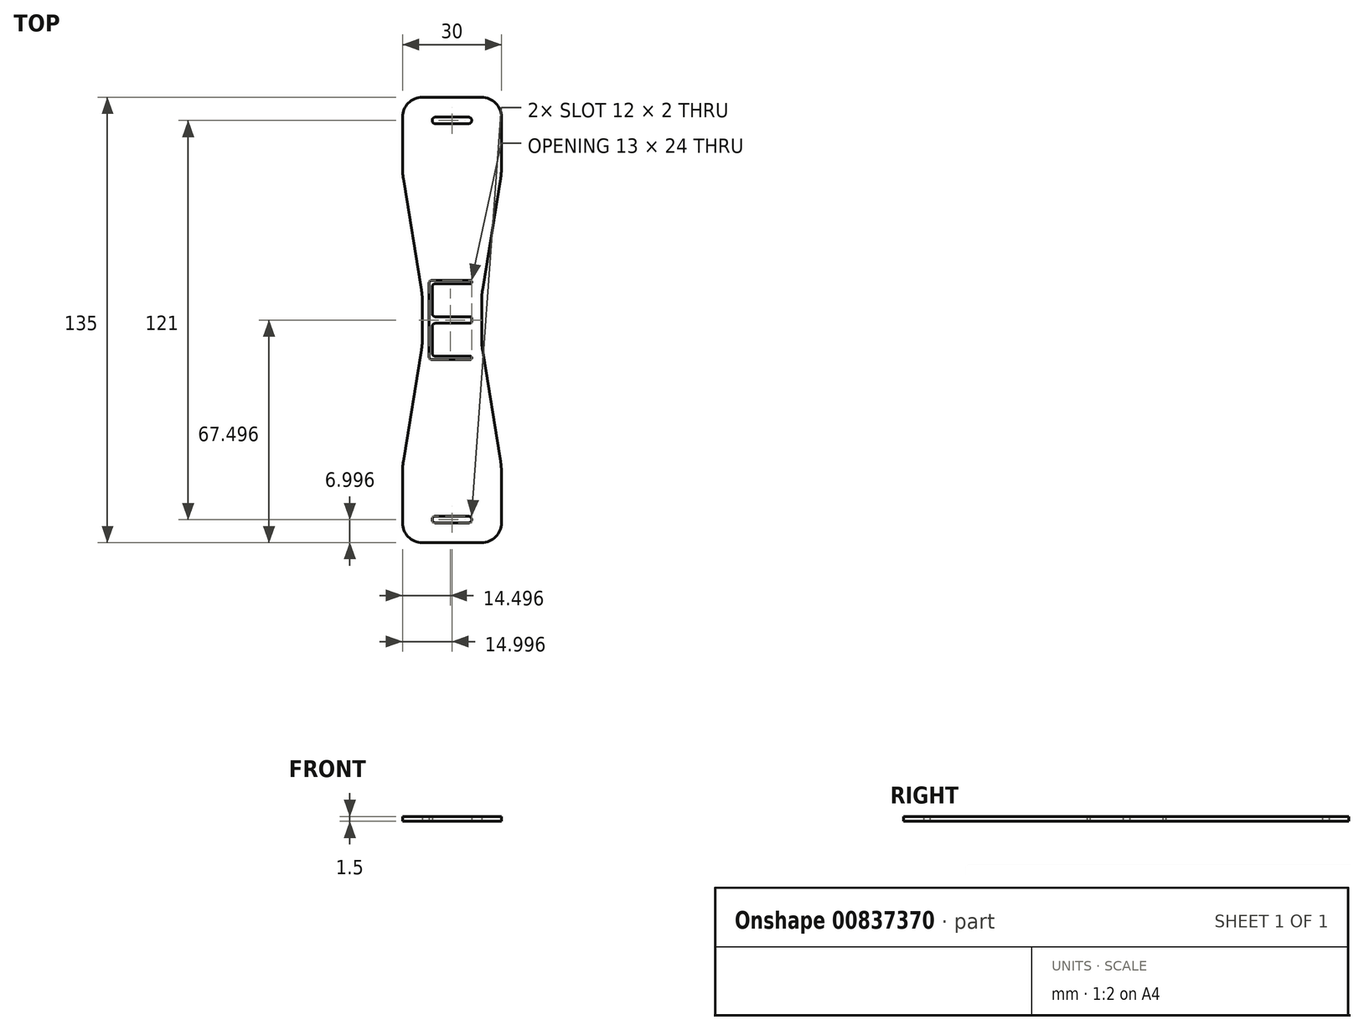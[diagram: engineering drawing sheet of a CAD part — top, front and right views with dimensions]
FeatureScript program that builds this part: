
annotation { "Feature Type Name" : "Feature", "Feature Type Description" : "" }
export const myFeature = defineFeature(function(context is Context, id is Id, definition is map)
    precondition{}
    {
        {
            var Q0;
            Q0=qCreatedBy(makeId("Top.planeOp"),FACE);
            var sketch = newSketch(context, id + "F0", { "sketchPlane" : qUnion([Q0])});
            skLineSegment(sketch, "E0.bottom", {"start": v(-13.76, 84.78) * mm, "end": v(16.24, 84.78) * mm});
            skLineSegment(sketch, "E0.top", {"start": v(-13.76, -50.22) * mm, "end": v(16.24, -50.22) * mm});
            skLineSegment(sketch, "E0.left", {"start": v(-13.76, 84.78) * mm, "end": v(-13.76, 61.78) * mm});
            skLineSegment(sketch, "E0.right", {"start": v(16.24, 84.78) * mm, "end": v(16.24, 61.78) * mm});
            skLineSegment(sketch, "E1.bottom", {"start": v(-3.76, 28.28) * mm, "end": v(6.74, 28.28) * mm});
            skLineSegment(sketch, "E1.top", {"start": v(-3.76, 18.28) * mm, "end": v(6.74, 18.28) * mm});
            skLineSegment(sketch, "E1.left", {"start": v(-4.76, 27.28) * mm, "end": v(-4.76, 19.28) * mm});
            skLineSegment(sketch, "E2.bottom", {"start": v(-3.76, 16.28) * mm, "end": v(6.74, 16.28) * mm});
            skLineSegment(sketch, "E2.top", {"start": v(-3.76, 6.28) * mm, "end": v(6.74, 6.28) * mm});
            skLineSegment(sketch, "E2.left", {"start": v(-4.76, 15.28) * mm, "end": v(-4.76, 7.28) * mm});
            skLineSegment(sketch, "E3.bottom", {"start": v(6.74, 29.28) * mm, "end": v(-4.76, 29.28) * mm});
            skLineSegment(sketch, "E3.left", {"start": v(7.24, 28.78) * mm, "end": v(7.24, 28.78) * mm});
            skLineSegment(sketch, "E3.right", {"start": v(-5.76, 28.28) * mm, "end": v(-5.76, 17.78) * mm});
            skLineSegment(sketch, "E4.top", {"start": v(6.74, 5.28) * mm, "end": v(-4.76, 5.28) * mm});
            skLineSegment(sketch, "E4.left", {"start": v(7.24, 16.78) * mm, "end": v(7.24, 16.28) * mm});
            skLineSegment(sketch, "E4.right", {"start": v(-5.76, 16.78) * mm, "end": v(-5.76, 6.28) * mm});
            skLineSegment(sketch, "E5.trimOffspring", {"start": v(7.24, 17.78) * mm, "end": v(7.24, 17.28) * mm});
            skLineSegment(sketch, "E6.trimOffspring", {"start": v(7.24, 5.78) * mm, "end": v(7.24, 5.78) * mm});
            skLineSegment(sketch, "E7.bottom", {"start": v(-3.76, -42.22) * mm, "end": v(6.24, -42.22) * mm});
            skLineSegment(sketch, "E7.top", {"start": v(-3.76, -44.22) * mm, "end": v(6.24, -44.22) * mm});
            skLineSegment(sketch, "E7.left", {"start": v(-4.76, -43.22) * mm, "end": v(-4.76, -43.22) * mm});
            skLineSegment(sketch, "E7.right", {"start": v(7.24, -43.22) * mm, "end": v(7.24, -43.22) * mm});
            skLineSegment(sketch, "E8.bottom", {"start": v(-3.76, 76.78) * mm, "end": v(6.24, 76.78) * mm});
            skLineSegment(sketch, "E8.top", {"start": v(-3.76, 78.78) * mm, "end": v(6.24, 78.78) * mm});
            skLineSegment(sketch, "E8.left", {"start": v(-4.76, 77.78) * mm, "end": v(-4.76, 77.78) * mm});
            skLineSegment(sketch, "E8.right", {"start": v(7.24, 77.78) * mm, "end": v(7.24, 77.78) * mm});
            skPoint(sketch, "E9.visualSharp", {"position": v(-4.76, 28.28) * mm});
            skArc(sketch, "E9.filletArc", {"start": v(-3.76, 28.28) * mm, "mid": v(-4.47, 27.98) * mm, "end": v(-4.76, 27.28) * mm});
            skPoint(sketch, "E10.visualSharp", {"position": v(-4.76, 18.28) * mm});
            skArc(sketch, "E10.filletArc", {"start": v(-4.76, 19.28) * mm, "mid": v(-4.47, 18.57) * mm, "end": v(-3.76, 18.28) * mm});
            skPoint(sketch, "E11.visualSharp", {"position": v(-5.76, 16.78) * mm});
            skPoint(sketch, "E12.visualSharp", {"position": v(-5.76, 29.28) * mm});
            skArc(sketch, "E12.filletArc", {"start": v(-4.76, 29.28) * mm, "mid": v(-5.47, 28.98) * mm, "end": v(-5.76, 28.28) * mm});
            skPoint(sketch, "E13.visualSharp", {"position": v(-4.76, 6.28) * mm});
            skArc(sketch, "E13.filletArc", {"start": v(-4.76, 7.28) * mm, "mid": v(-4.47, 6.57) * mm, "end": v(-3.76, 6.28) * mm});
            skPoint(sketch, "E14.visualSharp", {"position": v(-5.76, 5.28) * mm});
            skArc(sketch, "E14.filletArc", {"start": v(-5.76, 6.28) * mm, "mid": v(-5.47, 5.57) * mm, "end": v(-4.76, 5.28) * mm});
            skPoint(sketch, "E15.visualSharp", {"position": v(-5.76, 17.28) * mm});
            skPoint(sketch, "E16.visualSharp", {"position": v(-4.76, 16.28) * mm});
            skArc(sketch, "E16.filletArc", {"start": v(-3.76, 16.28) * mm, "mid": v(-4.47, 15.98) * mm, "end": v(-4.76, 15.28) * mm});
            skPoint(sketch, "E17.visualSharp", {"position": v(7.24, 16.28) * mm});
            skArc(sketch, "E17.filletArc", {"start": v(6.74, 16.28) * mm, "mid": v(7.09, 16.42) * mm, "end": v(7.24, 16.78) * mm});
            skPoint(sketch, "E18.visualSharp", {"position": v(7.24, 16.78) * mm});
            skPoint(sketch, "E19.visualSharp", {"position": v(7.24, 5.28) * mm});
            skArc(sketch, "E19.filletArc", {"start": v(6.74, 5.28) * mm, "mid": v(7.09, 5.42) * mm, "end": v(7.24, 5.78) * mm});
            skPoint(sketch, "E20.visualSharp", {"position": v(7.24, 6.28) * mm});
            skArc(sketch, "E20.filletArc", {"start": v(7.24, 5.78) * mm, "mid": v(7.09, 6.13) * mm, "end": v(6.74, 6.28) * mm});
            skPoint(sketch, "E21.visualSharp", {"position": v(7.24, 28.28) * mm});
            skArc(sketch, "E21.filletArc", {"start": v(6.74, 28.28) * mm, "mid": v(7.09, 28.42) * mm, "end": v(7.24, 28.78) * mm});
            skPoint(sketch, "E22.visualSharp", {"position": v(7.24, 29.28) * mm});
            skArc(sketch, "E22.filletArc", {"start": v(7.24, 28.78) * mm, "mid": v(7.09, 29.13) * mm, "end": v(6.74, 29.28) * mm});
            skPoint(sketch, "E23.visualSharp", {"position": v(7.24, 17.28) * mm});
            skPoint(sketch, "E24.visualSharp", {"position": v(7.24, 18.28) * mm});
            skArc(sketch, "E24.filletArc", {"start": v(7.24, 17.78) * mm, "mid": v(7.09, 18.13) * mm, "end": v(6.74, 18.28) * mm});
            skPoint(sketch, "E25.visualSharp", {"position": v(7.24, -42.22) * mm});
            skArc(sketch, "E25.filletArc", {"start": v(7.24, -43.22) * mm, "mid": v(6.94, -42.52) * mm, "end": v(6.24, -42.22) * mm});
            skPoint(sketch, "E26.visualSharp", {"position": v(7.24, -44.22) * mm});
            skArc(sketch, "E26.filletArc", {"start": v(6.24, -44.22) * mm, "mid": v(6.94, -43.93) * mm, "end": v(7.24, -43.22) * mm});
            skPoint(sketch, "E27.visualSharp", {"position": v(-4.76, -44.22) * mm});
            skArc(sketch, "E27.filletArc", {"start": v(-4.76, -43.22) * mm, "mid": v(-4.47, -43.93) * mm, "end": v(-3.76, -44.22) * mm});
            skPoint(sketch, "E28.visualSharp", {"position": v(-4.76, -42.22) * mm});
            skArc(sketch, "E28.filletArc", {"start": v(-3.76, -42.22) * mm, "mid": v(-4.47, -42.52) * mm, "end": v(-4.76, -43.22) * mm});
            skPoint(sketch, "E29.visualSharp", {"position": v(-4.76, 78.78) * mm});
            skArc(sketch, "E29.filletArc", {"start": v(-3.76, 78.78) * mm, "mid": v(-4.47, 78.48) * mm, "end": v(-4.76, 77.78) * mm});
            skPoint(sketch, "E30.visualSharp", {"position": v(-4.76, 76.78) * mm});
            skArc(sketch, "E30.filletArc", {"start": v(-4.76, 77.78) * mm, "mid": v(-4.47, 77.07) * mm, "end": v(-3.76, 76.78) * mm});
            skPoint(sketch, "E31.visualSharp", {"position": v(7.24, 76.78) * mm});
            skArc(sketch, "E31.filletArc", {"start": v(6.24, 76.78) * mm, "mid": v(6.94, 77.07) * mm, "end": v(7.24, 77.78) * mm});
            skPoint(sketch, "E32.visualSharp", {"position": v(7.24, 78.78) * mm});
            skArc(sketch, "E32.filletArc", {"start": v(7.24, 77.78) * mm, "mid": v(6.94, 78.48) * mm, "end": v(6.24, 78.78) * mm});
            skLineSegment(sketch, "E33", {"start": v(-13.76, 61.78) * mm, "end": v(-7.76, 24.78) * mm});
            skLineSegment(sketch, "E34", {"start": v(-7.76, 24.78) * mm, "end": v(-7.76, 9.78) * mm});
            skLineSegment(sketch, "E35", {"start": v(-7.76, 9.78) * mm, "end": v(-13.76, -27.22) * mm});
            skLineSegment(sketch, "E36", {"start": v(16.24, 61.78) * mm, "end": v(10.24, 24.78) * mm});
            skLineSegment(sketch, "E37", {"start": v(10.24, 24.78) * mm, "end": v(10.24, 9.78) * mm});
            skLineSegment(sketch, "E38", {"start": v(10.24, 9.78) * mm, "end": v(16.24, -27.22) * mm});
            skLineSegment(sketch, "E39.trimOffspring", {"start": v(16.24, -27.22) * mm, "end": v(16.24, -50.22) * mm});
            skPoint(sketch, "E40.left.end.orphan", {"position": v(-13.76, 9.78) * mm});
            skPoint(sketch, "E40.left.start.orphan", {"position": v(-13.76, 24.78) * mm});
            skLineSegment(sketch, "E41.trimOffspring", {"start": v(-13.76, -27.22) * mm, "end": v(-13.76, -50.22) * mm});
            skLineSegment(sketch, "E42", {"start": v(-5.76, 17.78) * mm, "end": v(-5.76, 16.78) * mm});
            skLineSegment(sketch, "E43", {"start": v(7.24, 17.28) * mm, "end": v(7.24, 16.28) * mm});
            skSolve(sketch);
        }
        {
            var Q0;
            Q0=qSketchRegion(id+"F0",true);
            extrude(context, id + "F1", {"entities" : qUnion([Q0]), "depth" : 1.5 * mm, "offsetDistance" : 25 * mm});
        }
        {
            var Q0;
            Q0=makeQuery(id+"F1.opExtrude","SWEPT_EDGE",EDGE,{"disambiguationData":[OSD([sQuery(id+"F0.wireOp",EDGE,"E0.bottom"),sQuery(id+"F0.wireOp",EDGE,"E0.right")])]});
            var Q1;
            Q1=makeQuery(id+"F1.opExtrude","SWEPT_EDGE",EDGE,{"disambiguationData":[OSD([sQuery(id+"F0.wireOp",EDGE,"E0.bottom"),sQuery(id+"F0.wireOp",EDGE,"E0.left")])]});
            var Q2;
            Q2=makeQuery(id+"F1.opExtrude","SWEPT_EDGE",EDGE,{"disambiguationData":[OSD([sQuery(id+"F0.wireOp",EDGE,"E0.top"),sQuery(id+"F0.wireOp",EDGE,"E41.trimOffspring")])]});
            var Q3;
            Q3=makeQuery(id+"F1.opExtrude","SWEPT_EDGE",EDGE,{"disambiguationData":[OSD([sQuery(id+"F0.wireOp",EDGE,"E0.top"),sQuery(id+"F0.wireOp",EDGE,"E39.trimOffspring")])]});
            fillet(context, id + "F2", {"entities" : qUnion([Q0, Q1, Q2, Q3]), "radius" : 6 * mm, "tangentPropagation" : true, "allowEdgeOverflow" : false});
        }
        {
            var Q0;
            Q0=makeQuery(id+"F1.opExtrude","SWEPT_EDGE",EDGE,{"disambiguationData":[OSD([sQuery(id+"F0.wireOp",EDGE,"E0.right"),sQuery(id+"F0.wireOp",EDGE,"E36")])]});
            var Q1;
            Q1=makeQuery(id+"F1.opExtrude","SWEPT_EDGE",EDGE,{"disambiguationData":[OSD([sQuery(id+"F0.wireOp",EDGE,"E0.left"),sQuery(id+"F0.wireOp",EDGE,"E33")])]});
            var Q2;
            Q2=makeQuery(id+"F1.opExtrude","SWEPT_EDGE",EDGE,{"disambiguationData":[OSD([sQuery(id+"F0.wireOp",EDGE,"E38"),sQuery(id+"F0.wireOp",EDGE,"E39.trimOffspring")])]});
            var Q3;
            Q3=makeQuery(id+"F1.opExtrude","SWEPT_EDGE",EDGE,{"disambiguationData":[OSD([sQuery(id+"F0.wireOp",EDGE,"E35"),sQuery(id+"F0.wireOp",EDGE,"E41.trimOffspring")])]});
            var Q4;
            Q4=makeQuery(id+"F1.opExtrude","SWEPT_EDGE",EDGE,{"disambiguationData":[OSD([sQuery(id+"F0.wireOp",EDGE,"E34"),sQuery(id+"F0.wireOp",EDGE,"E35")])]});
            var Q5;
            Q5=makeQuery(id+"F1.opExtrude","SWEPT_EDGE",EDGE,{"disambiguationData":[OSD([sQuery(id+"F0.wireOp",EDGE,"E37"),sQuery(id+"F0.wireOp",EDGE,"E38")])]});
            var Q6;
            Q6=makeQuery(id+"F1.opExtrude","SWEPT_EDGE",EDGE,{"disambiguationData":[OSD([sQuery(id+"F0.wireOp",EDGE,"E36"),sQuery(id+"F0.wireOp",EDGE,"E37")])]});
            var Q7;
            Q7=makeQuery(id+"F1.opExtrude","SWEPT_EDGE",EDGE,{"disambiguationData":[OSD([sQuery(id+"F0.wireOp",EDGE,"E33"),sQuery(id+"F0.wireOp",EDGE,"E34")])]});
            fillet(context, id + "F3", {"entities" : qUnion([Q0, Q1, Q2, Q3, Q4, Q5, Q6, Q7]), "radius" : 20 * mm, "tangentPropagation" : true, "allowEdgeOverflow" : false});
        }
    });
